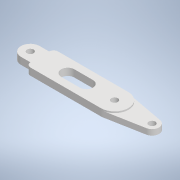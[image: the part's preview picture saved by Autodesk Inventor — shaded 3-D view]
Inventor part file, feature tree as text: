
AUTODESK INVENTOR PART (.ipt)
format: ipt  version: 2021 (Build 250183000, 183)  size: 192,512 bytes
history: native  units: mm
features: extrude x3, sketch x3, direct_edit x1, move_body x1
ambient origin geometry x8: Origin, YZ Plane, XZ Plane, XY Plane, X Axis, Y Axis, Z Axis, Center Point
bodies: Solid1 (feature_tree)
feature tree (8):
  extrude  "Extrusion1"  Depth=3.5mm
  extrude  "Extrusion4"  Depth=14.8mm
  extrude  "Extrusion5"  Depth=5.0mm
  direct_edit  "Direct Edit1"
  sketch  "Sketch1"  dims[d3=10.0mm d4=3.5mm]
  sketch  "Sketch4"  dims[d5=3.5mm d6=14.8mm]
  sketch  "Sketch5"  dims[d10=10.0mm d11=5.0mm d12=3.5mm d13=2.5mm d18=3.8mm d19=0.0mm d51=15.0mm d52=40.0mm d53=3.5mm d54=7.5mm d55=20.0mm d56=10.0mm d57=3.5mm d58=3.5mm d59=14.8mm d60=10.0mm d61=5.0mm d62=3.5mm d63=2.5mm d64=15.0mm d65=40.0mm d66=3.5mm d67=7.5mm d68=20.0mm d69=1.1mm d70=1.9mm d71=0.0mm d72=0.0mm d73=10.0mm d74=3.5mm d75=3.5mm d76=14.8mm d77=10.0mm d78=5.0mm d79=3.5mm d80=2.5mm d81=15.0mm d82=40.0mm d83=3.5mm d84=7.5mm d85=20.0mm d86=1.9mm d87=0.8mm d88=0.0mm d89=0.0mm d90=0.0mm d91=0.0mm d92=0.1mm d20=0.5mm d21=0.872665mm]
  move_body  "Move1"
